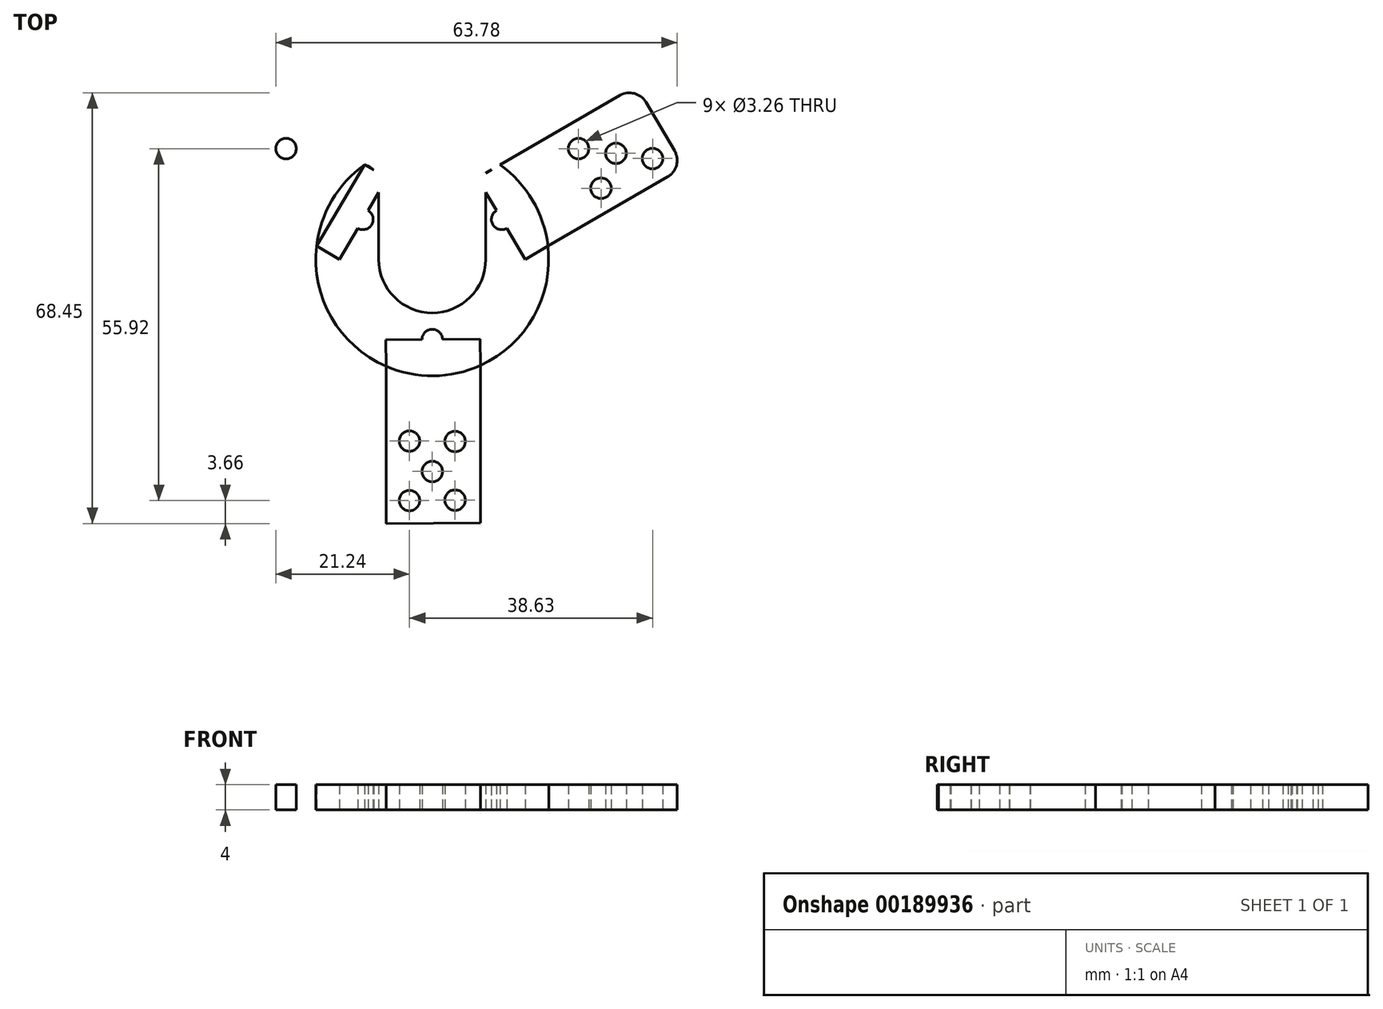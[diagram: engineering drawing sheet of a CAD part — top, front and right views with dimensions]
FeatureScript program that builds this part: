
annotation { "Feature Type Name" : "Feature", "Feature Type Description" : "" }
export const myFeature = defineFeature(function(context is Context, id is Id, definition is map)
    precondition{}
    {
        {
            var Q0;
            Q0=qCreatedBy(makeId("Top.planeOp"),FACE);
            var sketch = newSketch(context, id + "F0", { "sketchPlane" : qUnion([Q0])});
            skCircle(sketch, "E0", {"center": v(0, 0) * mm, "radius": 8.5 * mm});
            skCircle(sketch, "E1", {"center": v(0, 0) * mm, "radius": 18.5 * mm});
            skLineSegment(sketch, "E2", {"start": v(0, 0) * mm, "end": v(69.28, 40) * mm, "construction": true});
            skLineSegment(sketch, "E3.bottom", {"start": v(-8.5, 0) * mm, "end": v(8.5, 0) * mm});
            skLineSegment(sketch, "E3.top", {"start": v(-8.5, 40) * mm, "end": v(8.5, 40) * mm});
            skLineSegment(sketch, "E3.left", {"start": v(-8.5, 0) * mm, "end": v(-8.5, 40) * mm});
            skLineSegment(sketch, "E3.right", {"start": v(8.5, 0) * mm, "end": v(8.5, 40) * mm});
            skCircle(sketch, "E4.MirrorC", {"center": v(31.31, 22.26) * mm, "radius": 1.63 * mm});
            skCircle(sketch, "E5.MirrorC", {"center": v(11.02, 6.36) * mm, "radius": 1.63 * mm});
            skLineSegment(sketch, "E6.MirrorCS", {"start": v(18.38, 2.13) * mm, "end": v(14.77, 0) * mm});
            skLineSegment(sketch, "E7.MirrorCS", {"start": v(7.15, 12.92) * mm, "end": v(10.76, 15.05) * mm});
            skLineSegment(sketch, "E8.MirrorCS", {"start": v(14.77, 0) * mm, "end": v(7.15, 12.92) * mm});
            skLineSegment(sketch, "E9.MirrorCS", {"start": v(18.38, 2.13) * mm, "end": v(10.76, 15.05) * mm});
            skLineSegment(sketch, "E10.MirrorCS", {"start": v(10.76, 15.05) * mm, "end": v(32.41, 27.55) * mm});
            skLineSegment(sketch, "E11.MirrorCS", {"start": v(18.38, 2.13) * mm, "end": v(40.03, 14.63) * mm});
            skLineSegment(sketch, "E12.MirrorCS", {"start": v(40.03, 14.63) * mm, "end": v(32.41, 27.55) * mm});
            skCircle(sketch, "E13.MirrorC", {"center": v(35, 16.02) * mm, "radius": 1.63 * mm});
            skCircle(sketch, "E14", {"center": v(29.19, 16.85) * mm, "radius": 1.63 * mm});
            skLineSegment(sketch, "E15", {"start": v(32.77, 10.43) * mm, "end": v(25.27, 23.42) * mm, "construction": true});
            skCircle(sketch, "E16.MirrorC", {"center": v(23.24, 17.6) * mm, "radius": 1.63 * mm});
            skCircle(sketch, "E17.MirrorC", {"center": v(26.81, 11.3) * mm, "radius": 1.63 * mm});
            skLineSegment(sketch, "E18.MirrorCS", {"start": v(0, 0) * mm, "end": v(-69.28, 40) * mm, "construction": true});
            skLineSegment(sketch, "E19.MirrorCS", {"start": v(0, 0) * mm, "end": v(-69.28, -40) * mm, "construction": true});
            skLineSegment(sketch, "E20.MirrorCS", {"start": v(0, 0) * mm, "end": v(69.28, -40) * mm, "construction": true});
            skLineSegment(sketch, "E21.MirrorCS", {"start": v(0, 0) * mm, "end": v(0, 80) * mm, "construction": true});
            skLineSegment(sketch, "E22.MirrorCS", {"start": v(0, 0) * mm, "end": v(0, -80) * mm, "construction": true});
            skLineSegment(sketch, "E23.MirrorCS", {"start": v(-18.38, 2.13) * mm, "end": v(-14.77, 0) * mm});
            skCircle(sketch, "E24.MirrorC", {"center": v(-23.24, 17.6) * mm, "radius": 1.63 * mm});
            skLineSegment(sketch, "E25.MirrorCS", {"start": v(-40.03, 14.63) * mm, "end": v(-32.41, 27.55) * mm});
            skCircle(sketch, "E26.MirrorC", {"center": v(-35, 16.02) * mm, "radius": 1.63 * mm});
            skCircle(sketch, "E27.MirrorC", {"center": v(-26.81, 11.3) * mm, "radius": 1.63 * mm});
            skLineSegment(sketch, "E28.MirrorCS", {"start": v(-18.38, 2.13) * mm, "end": v(-40.03, 14.63) * mm});
            skCircle(sketch, "E29.MirrorC", {"center": v(-29.19, 16.85) * mm, "radius": 1.63 * mm});
            skCircle(sketch, "E30.MirrorC", {"center": v(-31.31, 22.26) * mm, "radius": 1.63 * mm});
            skLineSegment(sketch, "E31.MirrorCS", {"start": v(-32.77, 10.43) * mm, "end": v(-25.27, 23.42) * mm, "construction": true});
            skLineSegment(sketch, "E32.MirrorCS", {"start": v(-10.76, 15.05) * mm, "end": v(-32.41, 27.55) * mm});
            skLineSegment(sketch, "E33.MirrorCS", {"start": v(-14.77, 0) * mm, "end": v(-7.15, 12.92) * mm});
            skLineSegment(sketch, "E34.MirrorCS", {"start": v(-18.38, 2.13) * mm, "end": v(-10.76, 15.05) * mm});
            skLineSegment(sketch, "E35.MirrorCS", {"start": v(-7.15, 12.92) * mm, "end": v(-10.76, 15.05) * mm});
            skCircle(sketch, "E36.MirrorC", {"center": v(-11.02, 6.36) * mm, "radius": 1.63 * mm});
            skLineSegment(sketch, "E37.MirrorCS", {"start": v(-7.35, -41.98) * mm, "end": v(7.65, -41.84) * mm});
            skLineSegment(sketch, "E38.MirrorCS", {"start": v(-7.35, -33.6) * mm, "end": v(7.65, -33.6) * mm, "construction": true});
            skCircle(sketch, "E39.MirrorC", {"center": v(0, -33.7) * mm, "radius": 1.63 * mm});
            skLineSegment(sketch, "E40.MirrorCS", {"start": v(7.65, -16.84) * mm, "end": v(7.65, -41.84) * mm});
            skLineSegment(sketch, "E41.MirrorCS", {"start": v(-7.35, -16.98) * mm, "end": v(-7.35, -41.98) * mm});
            skCircle(sketch, "E42.MirrorC", {"center": v(0, -12.73) * mm, "radius": 1.63 * mm});
            skCircle(sketch, "E43.MirrorC", {"center": v(3.62, -38.25) * mm, "radius": 1.63 * mm});
            skLineSegment(sketch, "E44.MirrorCS", {"start": v(-7.35, -16.98) * mm, "end": v(7.65, -16.84) * mm});
            skCircle(sketch, "E45.MirrorC", {"center": v(-3.63, -38.32) * mm, "radius": 1.63 * mm});
            skCircle(sketch, "E46.MirrorC", {"center": v(3.62, -28.93) * mm, "radius": 1.63 * mm});
            skCircle(sketch, "E47.MirrorC", {"center": v(-3.63, -28.87) * mm, "radius": 1.63 * mm});
            skLineSegment(sketch, "E48.MirrorCS", {"start": v(-7.39, -12.8) * mm, "end": v(7.61, -12.66) * mm});
            skLineSegment(sketch, "E49.MirrorCS", {"start": v(-7.35, -16.98) * mm, "end": v(-7.39, -12.8) * mm});
            skLineSegment(sketch, "E50.MirrorCS", {"start": v(7.61, -12.66) * mm, "end": v(7.65, -16.84) * mm});
            skSolve(sketch);
        }
        {
            var Q0;
            {var subQ0=sQuery(id+"F0.wireOp",EDGE,"WSCxfVUN-meaz-QDOu-QnNy-QRzvSIZDZ6VB.bottom");Q0=makeQuery(id+"F0.imprint","IMPRINT",FACE,{"disambiguationData":[TD([[makeQuery(id+"F0.imprint","IMPRINT",EDGE,{"derivedFrom":subQ0}),-1.0]])]});}
            var Q1;
            Q1=makeQuery(id+"F0.imprint","IMPRINT",FACE,{"disambiguationData":[TD([[makeQuery(id+"F0.imprint","IMPRINT",EDGE,{"derivedFrom":sQuery(id+"F0.wireOp",EDGE,"WSCxfVUN-meaz-QDOu-QnNy-QRzvSIZDZ6VB.top")}),1.0]])]});
            var Q2;
            Q2=makeQuery(id+"F0.imprint","IMPRINT",FACE,{"disambiguationData":[TD([[makeQuery(id+"F0.imprint","IMPRINT",EDGE,{"derivedFrom":sQuery(id+"F0.wireOp",EDGE,"f0ca8109-8534-44e1-b6a6-f00158a75cb81.MirrorCS")}),-1.0]])]});
            var Q3;
            {var subQ0=sQuery(id+"F0.wireOp",EDGE,"8bebe3c3-a620-4855-813b-19bf353030e81.MirrorCS");Q3=makeQuery(id+"F0.imprint","IMPRINT",FACE,{"disambiguationData":[TD([[makeQuery(id+"F0.imprint","IMPRINT",EDGE,{"derivedFrom":subQ0}),-1.0]])]});}
            var Q4;
            {var subQ0=sQuery(id+"F0.wireOp",EDGE,"8bebe3c3-a620-4855-813b-19bf353030e80.MirrorCS");Q4=makeQuery(id+"F0.imprint","IMPRINT",FACE,{"disambiguationData":[TD([[makeQuery(id+"F0.imprint","IMPRINT",EDGE,{"derivedFrom":subQ0}),1.0]])]});}
            var Q5;
            {var subQ0=sQuery(id+"F0.wireOp",EDGE,"WSCxfVUN-meaz-QDOu-QnNy-QRzvSIZDZ6VB.bottom");var subQ5=sQuery(id+"F0.wireOp",EDGE,"YaanTXKd-sbEj-Zcqq-0OIl-obntNTxhTGOp");var subQ7=makeQuery(id+"F0.imprint","INTERSECT",VERTEX,{"disambiguationData":[OD(1.0)],"derivedFrom":[subQ0,subQ5]});Q5=makeQuery(id+"F0.imprint","IMPRINT",FACE,{"disambiguationData":[TD([[makeQuery(id+"F0.imprint","IMPRINT",EDGE,{"disambiguationData":[TD([[subQ7,1.0]])],"derivedFrom":subQ5}),-1.0]])]});}
            var Q6;
            {var subQ0=sQuery(id+"F0.wireOp",EDGE,"WSCxfVUN-meaz-QDOu-QnNy-QRzvSIZDZ6VB.bottom");var subQ5=sQuery(id+"F0.wireOp",EDGE,"YaanTXKd-sbEj-Zcqq-0OIl-obntNTxhTGOp");var subQ7=makeQuery(id+"F0.imprint","INTERSECT",VERTEX,{"disambiguationData":[OD(0.0)],"derivedFrom":[subQ0,subQ5]});Q6=makeQuery(id+"F0.imprint","IMPRINT",FACE,{"disambiguationData":[TD([[makeQuery(id+"F0.imprint","IMPRINT",EDGE,{"disambiguationData":[TD([[subQ7,-1.0]])],"derivedFrom":subQ5}),-1.0]])]});}
            var Q7;
            {var subQ1=sQuery(id+"F0.wireOp",EDGE,"E1");var subQ3=sQuery(id+"F0.wireOp",EDGE,"tnyU2rVy-d4gK-21wb-KfcG-GGYwWitywWsr");var subQ4=makeQuery(id+"F0.imprint","INTERSECT",VERTEX,{"disambiguationData":[OD(1.0)],"derivedFrom":[subQ1,subQ3]});Q7=makeQuery(id+"F0.imprint","IMPRINT",FACE,{"disambiguationData":[TD([[makeQuery(id+"F0.imprint","IMPRINT",EDGE,{"disambiguationData":[TD([[subQ4,-1.0]])],"derivedFrom":subQ3}),-1.0]])]});}
            var Q8;
            {var subQ1=sQuery(id+"F0.wireOp",EDGE,"E1");var subQ3=sQuery(id+"F0.wireOp",EDGE,"tnyU2rVy-d4gK-21wb-KfcG-GGYwWitywWsr");var subQ4=makeQuery(id+"F0.imprint","INTERSECT",VERTEX,{"disambiguationData":[OD(0.0)],"derivedFrom":[subQ1,subQ3]});Q8=makeQuery(id+"F0.imprint","IMPRINT",FACE,{"disambiguationData":[TD([[makeQuery(id+"F0.imprint","IMPRINT",EDGE,{"disambiguationData":[TD([[subQ4,1.0]])],"derivedFrom":subQ3}),-1.0]])]});}
            var Q9;
            {var subQ0=sQuery(id+"F0.wireOp",EDGE,"5zwkFa9z-vczj-OBVo-oIgf-nvGZTg8HBam4");Q9=makeQuery(id+"F0.imprint","IMPRINT",FACE,{"disambiguationData":[TD([[makeQuery(id+"F0.imprint","IMPRINT",EDGE,{"derivedFrom":subQ0}),1.0]])]});}
            var Q10;
            {var subQ0=sQuery(id+"F0.wireOp",EDGE,"Eu31YCNJ-Q31v-MGss-Lh4a-CA6DCSBlaLMu");var subQ1=sQuery(id+"F0.wireOp",EDGE,"f0ca8109-8534-44e1-b6a6-f00158a75cb80.MirrorCS");var subQ2=makeQuery(id+"F0.imprint","INTERSECT",VERTEX,{"disambiguationData":[OD(0.0)],"derivedFrom":[subQ1,subQ0]});Q10=makeQuery(id+"F0.imprint","IMPRINT",FACE,{"disambiguationData":[TD([[makeQuery(id+"F0.imprint","IMPRINT",EDGE,{"disambiguationData":[TD([[subQ2,-1.0]])],"derivedFrom":subQ1}),-1.0]])]});}
            var Q11;
            {var subQ3=sQuery(id+"F0.wireOp",EDGE,"PdqkOLUQ-Barv-RhwF-eB8Z-qnaO4HOZ3Eg8");var subQ7=sQuery(id+"F0.wireOp",EDGE,"44e218f5-b77e-4724-b564-b3afd1cfe93b0.MirrorC");var subQ8=makeQuery(id+"F0.imprint","INTERSECT",VERTEX,{"disambiguationData":[OD(0.0)],"derivedFrom":[subQ7,subQ3]});Q11=makeQuery(id+"F0.imprint","IMPRINT",FACE,{"disambiguationData":[TD([[makeQuery(id+"F0.imprint","IMPRINT",EDGE,{"disambiguationData":[TD([[subQ8,1.0]])],"derivedFrom":subQ7}),1.0]])]});}
            var Q12;
            {var subQ3=sQuery(id+"F0.wireOp",EDGE,"tnyU2rVy-d4gK-21wb-KfcG-GGYwWitywWsr");var subQ5=sQuery(id+"F0.wireOp",EDGE,"E3.left");var subQ6=makeQuery(id+"F0.imprint","INTERSECT",VERTEX,{"disambiguationData":[OD(1.0)],"derivedFrom":[subQ5,subQ3]});Q12=makeQuery(id+"F0.imprint","IMPRINT",FACE,{"disambiguationData":[TD([[makeQuery(id+"F0.imprint","IMPRINT",EDGE,{"disambiguationData":[TD([[subQ6,-1.0]])],"derivedFrom":subQ5}),1.0]])]});}
            var Q13;
            {var subQ13=sQuery(id+"F0.wireOp",EDGE,"5zwkFa9z-vczj-OBVo-oIgf-nvGZTg8HBam4");Q13=makeQuery(id+"F0.imprint","IMPRINT",FACE,{"disambiguationData":[TD([[makeQuery(id+"F0.imprint","IMPRINT",EDGE,{"derivedFrom":subQ13}),-1.0]])]});}
            var Q14;
            {var subQ10=sQuery(id+"F0.wireOp",EDGE,"ad4cd247-eadd-4092-a59b-e7cfdbcd3d190.MirrorCS");Q14=makeQuery(id+"F0.imprint","IMPRINT",FACE,{"disambiguationData":[TD([[makeQuery(id+"F0.imprint","IMPRINT",EDGE,{"derivedFrom":subQ10}),1.0]])]});}
            var Q15;
            {var subQ0=sQuery(id+"F0.wireOp",EDGE,"96472c90-df4f-483d-8e78-cde8d417d6a10.MirrorC");var subQ1=sQuery(id+"F0.wireOp",EDGE,"E3.right");var subQ2=makeQuery(id+"F0.imprint","INTERSECT",VERTEX,{"disambiguationData":[OD(1.0)],"derivedFrom":[subQ1,subQ0]});Q15=makeQuery(id+"F0.imprint","IMPRINT",FACE,{"disambiguationData":[TD([[makeQuery(id+"F0.imprint","IMPRINT",EDGE,{"disambiguationData":[TD([[subQ2,-1.0]])],"derivedFrom":subQ1}),-1.0]])]});}
            var Q16;
            {var subQ0=sQuery(id+"F0.wireOp",EDGE,"96472c90-df4f-483d-8e78-cde8d417d6a10.MirrorC");var subQ1=sQuery(id+"F0.wireOp",EDGE,"8bebe3c3-a620-4855-813b-19bf353030e80.MirrorCS");var subQ2=makeQuery(id+"F0.imprint","INTERSECT",VERTEX,{"disambiguationData":[OD(1.0)],"derivedFrom":[subQ1,subQ0]});Q16=makeQuery(id+"F0.imprint","IMPRINT",FACE,{"disambiguationData":[TD([[makeQuery(id+"F0.imprint","IMPRINT",EDGE,{"disambiguationData":[TD([[subQ2,-1.0]])],"derivedFrom":subQ1}),-1.0]])]});}
            var Q17;
            {var subQ1=sQuery(id+"F0.wireOp",EDGE,"E1");var subQ3=sQuery(id+"F0.wireOp",EDGE,"96472c90-df4f-483d-8e78-cde8d417d6a10.MirrorC");var subQ4=makeQuery(id+"F0.imprint","INTERSECT",VERTEX,{"disambiguationData":[OD(0.0)],"derivedFrom":[subQ1,subQ3]});Q17=makeQuery(id+"F0.imprint","IMPRINT",FACE,{"disambiguationData":[TD([[makeQuery(id+"F0.imprint","IMPRINT",EDGE,{"disambiguationData":[TD([[subQ4,-1.0]])],"derivedFrom":subQ3}),1.0]])]});}
            var Q18;
            {var subQ6=sQuery(id+"F0.wireOp",EDGE,"8bebe3c3-a620-4855-813b-19bf353030e80.MirrorCS");var subQ9=sQuery(id+"F0.wireOp",EDGE,"eb3548f0-c353-4ace-a271-4014bca6502c0.MirrorCS");var subQ11=makeQuery(id+"F0.imprint","INTERSECT",VERTEX,{"derivedFrom":[subQ6,subQ9]});Q18=makeQuery(id+"F0.imprint","IMPRINT",FACE,{"disambiguationData":[TD([[makeQuery(id+"F0.imprint","IMPRINT",EDGE,{"disambiguationData":[TD([[subQ11,-1.0]])],"derivedFrom":subQ6}),-1.0]])]});}
            var Q19;
            {var subQ4=sQuery(id+"F0.wireOp",EDGE,"98e411e3-b966-48b7-8edd-d8c682f9ff5b0.MirrorC");var subQ5=sQuery(id+"F0.wireOp",EDGE,"E3.right");var subQ6=makeQuery(id+"F0.imprint","INTERSECT",VERTEX,{"disambiguationData":[OD(0.0)],"derivedFrom":[subQ5,subQ4]});Q19=makeQuery(id+"F0.imprint","IMPRINT",FACE,{"disambiguationData":[TD([[makeQuery(id+"F0.imprint","IMPRINT",EDGE,{"disambiguationData":[TD([[subQ6,-1.0]])],"derivedFrom":subQ5}),-1.0]])]});}
            var Q20;
            {var subQ0=sQuery(id+"F0.wireOp",EDGE,"tnyU2rVy-d4gK-21wb-KfcG-GGYwWitywWsr");var subQ1=sQuery(id+"F0.wireOp",EDGE,"E3.left");var subQ2=makeQuery(id+"F0.imprint","INTERSECT",VERTEX,{"disambiguationData":[OD(0.0)],"derivedFrom":[subQ1,subQ0]});Q20=makeQuery(id+"F0.imprint","IMPRINT",FACE,{"disambiguationData":[TD([[makeQuery(id+"F0.imprint","IMPRINT",EDGE,{"disambiguationData":[TD([[subQ2,-1.0]])],"derivedFrom":subQ1}),1.0]])]});}
            var Q21;
            {var subQ0=sQuery(id+"F0.wireOp",EDGE,"Eu31YCNJ-Q31v-MGss-Lh4a-CA6DCSBlaLMu");var subQ1=sQuery(id+"F0.wireOp",EDGE,"E3.left");var subQ2=makeQuery(id+"F0.imprint","INTERSECT",VERTEX,{"disambiguationData":[OD(1.0)],"derivedFrom":[subQ1,subQ0]});Q21=makeQuery(id+"F0.imprint","IMPRINT",FACE,{"disambiguationData":[TD([[makeQuery(id+"F0.imprint","IMPRINT",EDGE,{"disambiguationData":[TD([[subQ2,-1.0]])],"derivedFrom":subQ1}),1.0]])]});}
            var Q22;
            {var subQ0=sQuery(id+"F0.wireOp",EDGE,"96472c90-df4f-483d-8e78-cde8d417d6a10.MirrorC");var subQ1=sQuery(id+"F0.wireOp",EDGE,"E3.right");var subQ2=makeQuery(id+"F0.imprint","INTERSECT",VERTEX,{"disambiguationData":[OD(0.0)],"derivedFrom":[subQ1,subQ0]});Q22=makeQuery(id+"F0.imprint","IMPRINT",FACE,{"disambiguationData":[TD([[makeQuery(id+"F0.imprint","IMPRINT",EDGE,{"disambiguationData":[TD([[subQ2,-1.0]])],"derivedFrom":subQ1}),-1.0]])]});}
            var Q23;
            {var subQ0=sQuery(id+"F0.wireOp",EDGE,"98e411e3-b966-48b7-8edd-d8c682f9ff5b0.MirrorC");var subQ1=sQuery(id+"F0.wireOp",EDGE,"E3.right");var subQ2=makeQuery(id+"F0.imprint","INTERSECT",VERTEX,{"disambiguationData":[OD(1.0)],"derivedFrom":[subQ1,subQ0]});Q23=makeQuery(id+"F0.imprint","IMPRINT",FACE,{"disambiguationData":[TD([[makeQuery(id+"F0.imprint","IMPRINT",EDGE,{"disambiguationData":[TD([[subQ2,-1.0]])],"derivedFrom":subQ1}),-1.0]])]});}
            var Q24;
            {var subQ0=sQuery(id+"F0.wireOp",EDGE,"ad4cd247-eadd-4092-a59b-e7cfdbcd3d190.MirrorCS");Q24=makeQuery(id+"F0.imprint","IMPRINT",FACE,{"disambiguationData":[TD([[makeQuery(id+"F0.imprint","IMPRINT",EDGE,{"derivedFrom":subQ0}),-1.0]])]});}
            var Q25;
            {var subQ1=sQuery(id+"F0.wireOp",EDGE,"E1");var subQ3=sQuery(id+"F0.wireOp",EDGE,"8e164b55-78fa-432d-9327-841eefd8ee400.MirrorC");var subQ4=makeQuery(id+"F0.imprint","INTERSECT",VERTEX,{"disambiguationData":[OD(1.0)],"derivedFrom":[subQ1,subQ3]});Q25=makeQuery(id+"F0.imprint","IMPRINT",FACE,{"disambiguationData":[TD([[makeQuery(id+"F0.imprint","IMPRINT",EDGE,{"disambiguationData":[TD([[subQ4,1.0]])],"derivedFrom":subQ3}),1.0]])]});}
            var Q26;
            {var subQ1=sQuery(id+"F0.wireOp",EDGE,"E1");var subQ3=sQuery(id+"F0.wireOp",EDGE,"8e164b55-78fa-432d-9327-841eefd8ee400.MirrorC");var subQ4=makeQuery(id+"F0.imprint","INTERSECT",VERTEX,{"disambiguationData":[OD(0.0)],"derivedFrom":[subQ1,subQ3]});Q26=makeQuery(id+"F0.imprint","IMPRINT",FACE,{"disambiguationData":[TD([[makeQuery(id+"F0.imprint","IMPRINT",EDGE,{"disambiguationData":[TD([[subQ4,-1.0]])],"derivedFrom":subQ3}),1.0]])]});}
            var Q27;
            {var subQ0=sQuery(id+"F0.wireOp",EDGE,"7314f42c-cad2-4172-aff1-629ba6ee1ebc0.MirrorCS");Q27=makeQuery(id+"F0.imprint","IMPRINT",FACE,{"disambiguationData":[TD([[makeQuery(id+"F0.imprint","IMPRINT",EDGE,{"derivedFrom":subQ0}),-1.0]])]});}
            var Q28;
            {var subQ0=sQuery(id+"F0.wireOp",EDGE,"5bc87236-34a1-477c-9ee7-68cee69442190.MirrorCS");var subQ1=sQuery(id+"F0.wireOp",EDGE,"e7bf57d9-860a-4b06-a2f3-e0c013f7b1730.MirrorC");var subQ2=makeQuery(id+"F0.imprint","INTERSECT",VERTEX,{"disambiguationData":[OD(0.0)],"derivedFrom":[subQ1,subQ0]});Q28=makeQuery(id+"F0.imprint","IMPRINT",FACE,{"disambiguationData":[TD([[makeQuery(id+"F0.imprint","IMPRINT",EDGE,{"disambiguationData":[TD([[subQ2,-1.0]])],"derivedFrom":subQ1}),-1.0]])]});}
            var Q29;
            {var subQ2=sQuery(id+"F0.wireOp",EDGE,"5bc87236-34a1-477c-9ee7-68cee69442190.MirrorCS");var subQ4=sQuery(id+"F0.wireOp",EDGE,"e7bf57d9-860a-4b06-a2f3-e0c013f7b1730.MirrorC");var subQ5=makeQuery(id+"F0.imprint","INTERSECT",VERTEX,{"disambiguationData":[OD(0.0)],"derivedFrom":[subQ4,subQ2]});Q29=makeQuery(id+"F0.imprint","IMPRINT",FACE,{"disambiguationData":[TD([[makeQuery(id+"F0.imprint","IMPRINT",EDGE,{"disambiguationData":[TD([[subQ5,1.0]])],"derivedFrom":subQ4}),-1.0]])]});}
            var Q30;
            {var subQ4=sQuery(id+"F0.wireOp",EDGE,"bqEZveQ3-onws-oIJp-lOEs-Z2oYY6Y2JLHC");Q30=makeQuery(id+"F0.imprint","IMPRINT",FACE,{"disambiguationData":[TD([[makeQuery(id+"F0.imprint","IMPRINT",EDGE,{"derivedFrom":subQ4}),1.0]])]});}
            var Q31;
            {var subQ0=sQuery(id+"F0.wireOp",EDGE,"E9.MirrorCS");Q31=makeQuery(id+"F0.imprint","IMPRINT",FACE,{"disambiguationData":[TD([[makeQuery(id+"F0.imprint","IMPRINT",EDGE,{"derivedFrom":subQ0}),-1.0]])]});}
            var Q32;
            {var subQ9=sQuery(id+"F0.wireOp",EDGE,"E6.MirrorCS");Q32=makeQuery(id+"F0.imprint","IMPRINT",FACE,{"disambiguationData":[TD([[makeQuery(id+"F0.imprint","IMPRINT",EDGE,{"derivedFrom":subQ9}),-1.0]])]});}
            var Q33;
            Q33=makeQuery(id+"F0.imprint","IMPRINT",FACE,{"disambiguationData":[TD([[makeQuery(id+"F0.imprint","IMPRINT",EDGE,{"derivedFrom":sQuery(id+"F0.wireOp",EDGE,"E4.MirrorC")}),1.0]])]});
            var Q34;
            {var subQ1=sQuery(id+"F0.wireOp",EDGE,"4d25dec2-b40e-4c05-a0ef-0114d6cd83c32.MirrorCS");Q34=makeQuery(id+"F0.imprint","IMPRINT",FACE,{"disambiguationData":[TD([[makeQuery(id+"F0.imprint","IMPRINT",EDGE,{"derivedFrom":subQ1}),-1.0]])]});}
            var Q35;
            {var subQ0=sQuery(id+"F0.wireOp",EDGE,"4d25dec2-b40e-4c05-a0ef-0114d6cd83c35.MirrorCS");Q35=makeQuery(id+"F0.imprint","IMPRINT",FACE,{"disambiguationData":[TD([[makeQuery(id+"F0.imprint","IMPRINT",EDGE,{"derivedFrom":subQ0}),-1.0]])]});}
            var Q36;
            Q36=makeQuery(id+"F0.imprint","IMPRINT",FACE,{"disambiguationData":[TD([[makeQuery(id+"F0.imprint","IMPRINT",EDGE,{"derivedFrom":sQuery(id+"F0.wireOp",EDGE,"4d25dec2-b40e-4c05-a0ef-0114d6cd83c30.MirrorC")}),1.0]])]});
            var Q37;
            {var subQ10=sQuery(id+"F0.wireOp",EDGE,"E6.MirrorCS");Q37=makeQuery(id+"F0.imprint","IMPRINT",FACE,{"disambiguationData":[TD([[makeQuery(id+"F0.imprint","IMPRINT",EDGE,{"derivedFrom":subQ10}),1.0]])]});}
            var Q38;
            {var subQ0=sQuery(id+"F0.wireOp",EDGE,"E49.MirrorCS");Q38=makeQuery(id+"F0.imprint","IMPRINT",FACE,{"disambiguationData":[TD([[makeQuery(id+"F0.imprint","IMPRINT",EDGE,{"derivedFrom":subQ0}),-1.0]])]});}
            var Q39;
            {var subQ0=sQuery(id+"F0.wireOp",EDGE,"E44.MirrorCS");var subQ1=sQuery(id+"F0.wireOp",EDGE,"E1");var subQ3=makeQuery(id+"F0.imprint","INTERSECT",VERTEX,{"derivedFrom":[subQ1,subQ0]});Q39=makeQuery(id+"F0.imprint","IMPRINT",FACE,{"disambiguationData":[TD([[makeQuery(id+"F0.imprint","IMPRINT",EDGE,{"disambiguationData":[TD([[subQ3,-1.0]])],"derivedFrom":subQ1}),-1.0]])]});}
            var Q40;
            {var subQ1=sQuery(id+"F0.wireOp",EDGE,"E23.MirrorCS");Q40=makeQuery(id+"F0.imprint","IMPRINT",FACE,{"disambiguationData":[TD([[makeQuery(id+"F0.imprint","IMPRINT",EDGE,{"derivedFrom":subQ1}),1.0]])]});}
            var Q41;
            {var subQ0=sQuery(id+"F0.wireOp",EDGE,"E1");var subQ1=sQuery(id+"F0.wireOp",EDGE,"E34.MirrorCS");var subQ3=makeQuery(id+"F0.imprint","INTERSECT",VERTEX,{"derivedFrom":[subQ1,subQ0]});Q41=makeQuery(id+"F0.imprint","IMPRINT",FACE,{"disambiguationData":[TD([[makeQuery(id+"F0.imprint","IMPRINT",EDGE,{"disambiguationData":[TD([[subQ3,1.0]])],"derivedFrom":subQ1}),1.0]])]});}
            var Q42;
            Q42=makeQuery(id+"F0.imprint","IMPRINT",FACE,{"disambiguationData":[TD([[makeQuery(id+"F0.imprint","IMPRINT",EDGE,{"derivedFrom":sQuery(id+"F0.wireOp",EDGE,"E24.MirrorC")}),1.0]])]});
            var Q43;
            Q43=makeQuery(id+"F0.imprint","IMPRINT",FACE,{"disambiguationData":[TD([[makeQuery(id+"F0.imprint","IMPRINT",EDGE,{"derivedFrom":sQuery(id+"F0.wireOp",EDGE,"E39.MirrorC")}),-1.0]])]});
            extrude(context, id + "F1", {"entities" : qUnion([Q0, Q1, Q2, Q3, Q4, Q5, Q6, Q7, Q8, Q9, Q10, Q11, Q12, Q13, Q14, Q15, Q16, Q17, Q18, Q19, Q20, Q21, Q22, Q23, Q24, Q25, Q26, Q27, Q28, Q29, Q30, Q31, Q32, Q33, Q34, Q35, Q36, Q37, Q38, Q39, Q40, Q41, Q42, Q43]), "depth" : 4 * mm});
        }
        {
            var Q0;
            Q0=makeQuery(id+"F1.opExtrude","SWEPT_EDGE",EDGE,{"disambiguationData":[OSD([sQuery(id+"F0.wireOp",EDGE,"f0ca8109-8534-44e1-b6a6-f00158a75cb81.MirrorCS"),sQuery(id+"F0.wireOp",EDGE,"f0ca8109-8534-44e1-b6a6-f00158a75cb82.MirrorCS")])]});
            var Q1;
            Q1=makeQuery(id+"F1.opExtrude","SWEPT_EDGE",EDGE,{"disambiguationData":[OSD([sQuery(id+"F0.wireOp",EDGE,"E10.MirrorCS"),sQuery(id+"F0.wireOp",EDGE,"E12.MirrorCS")])]});
            var Q2;
            Q2=makeQuery(id+"F1.opExtrude","SWEPT_EDGE",EDGE,{"disambiguationData":[OSD([sQuery(id+"F0.wireOp",EDGE,"E11.MirrorCS"),sQuery(id+"F0.wireOp",EDGE,"E12.MirrorCS")])]});
            var Q3;
            Q3=makeQuery(id+"F1.opExtrude","SWEPT_EDGE",EDGE,{"disambiguationData":[OSD([sQuery(id+"F0.wireOp",EDGE,"f0ca8109-8534-44e1-b6a6-f00158a75cb81.MirrorCS"),sQuery(id+"F0.wireOp",EDGE,"f0ca8109-8534-44e1-b6a6-f00158a75cb83.MirrorCS")])]});
            var Q4;
            Q4=makeQuery(id+"F1.opExtrude","SWEPT_EDGE",EDGE,{"disambiguationData":[OSD([sQuery(id+"F0.wireOp",EDGE,"4d25dec2-b40e-4c05-a0ef-0114d6cd83c37.MirrorCS"),sQuery(id+"F0.wireOp",EDGE,"4d25dec2-b40e-4c05-a0ef-0114d6cd83c38.MirrorCS")])]});
            var Q5;
            Q5=makeQuery(id+"F1.opExtrude","SWEPT_EDGE",EDGE,{"disambiguationData":[OSD([sQuery(id+"F0.wireOp",EDGE,"4d25dec2-b40e-4c05-a0ef-0114d6cd83c36.MirrorCS"),sQuery(id+"F0.wireOp",EDGE,"4d25dec2-b40e-4c05-a0ef-0114d6cd83c37.MirrorCS")])]});
            var Q6;
            Q6=makeQuery(id+"F1.opExtrude","SWEPT_EDGE",EDGE,{"disambiguationData":[OSD([sQuery(id+"F0.wireOp",EDGE,"E1"),sQuery(id+"F0.wireOp",EDGE,"E3.right")])]});
            var Q7;
            Q7=makeQuery(id+"F1.opExtrude","SWEPT_EDGE",EDGE,{"disambiguationData":[OSD([sQuery(id+"F0.wireOp",EDGE,"E1"),sQuery(id+"F0.wireOp",EDGE,"E3.left")])]});
            fillet(context, id + "F2", {"entities" : qUnion([Q0, Q1, Q2, Q3, Q4, Q5, Q6, Q7]), "radius" : 3 * mm, "tangentPropagation" : true, "allowEdgeOverflow" : false});
        }
    });
